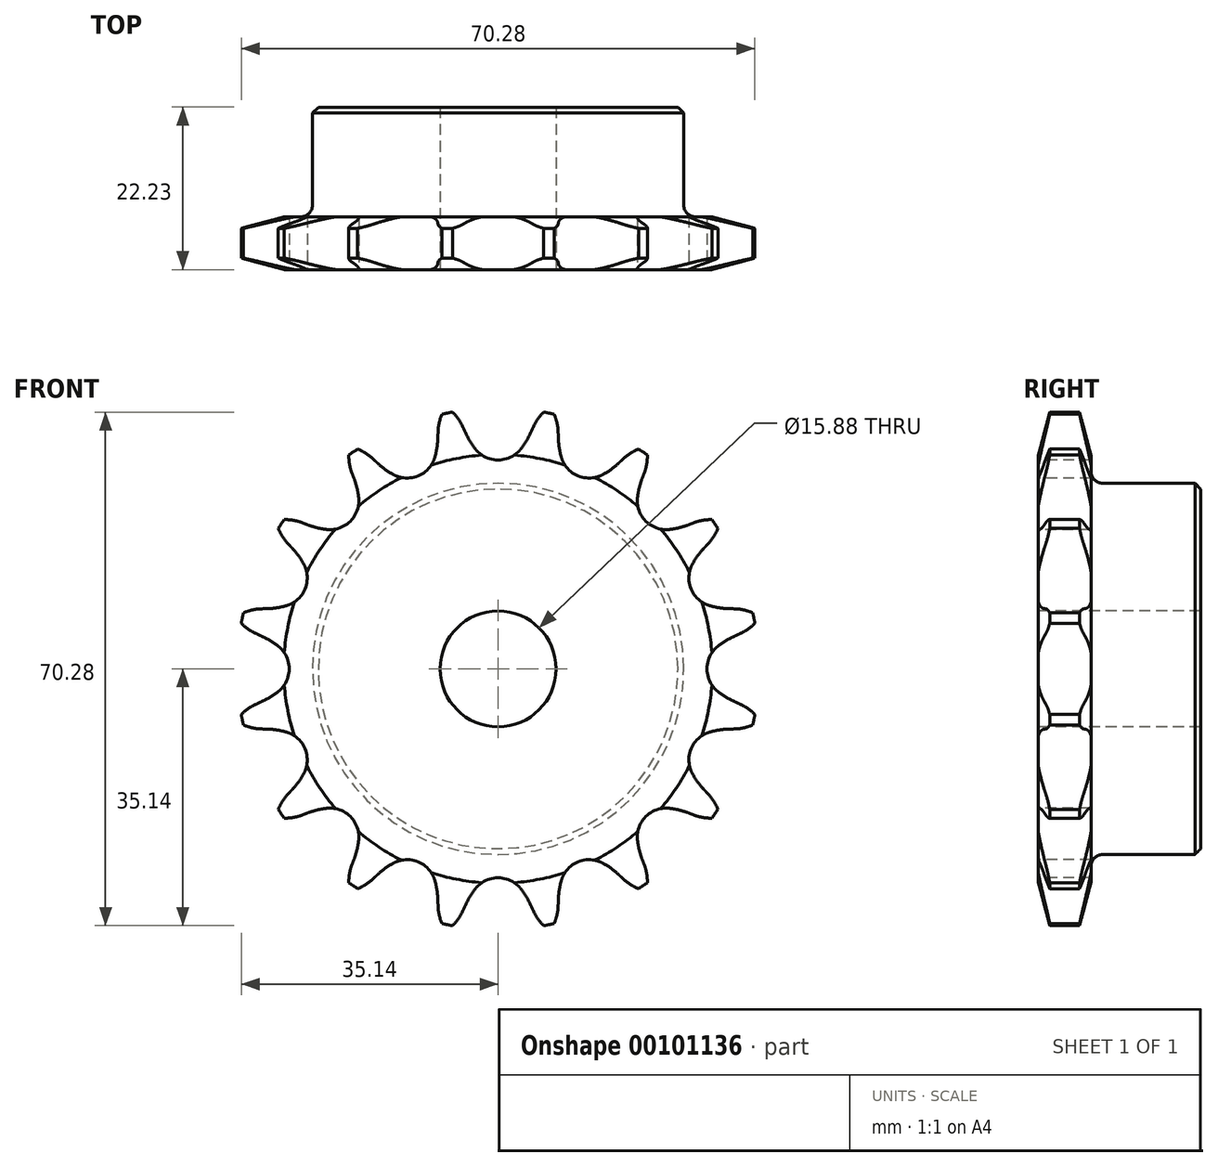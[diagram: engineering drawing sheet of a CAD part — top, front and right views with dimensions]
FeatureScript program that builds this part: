
annotation { "Feature Type Name" : "Feature", "Feature Type Description" : "" }
export const myFeature = defineFeature(function(context is Context, id is Id, definition is map)
    precondition{}
    {
        {
            var Q0;
            Q0=qCreatedBy(makeId("Right.planeOp"),FACE);
            var sketch = newSketch(context, id + "F0", { "sketchPlane" : qUnion([Q0])});
            skLineSegment(sketch, "E0", {"start": v(0, 0) * mm, "end": v(22.23, 0) * mm, "construction": true});
            skLineSegment(sketch, "E1.bottom", {"start": v(0, 7.94) * mm, "end": v(7.21, 7.94) * mm});
            skLineSegment(sketch, "E1.top", {"start": v(0, 35.69) * mm, "end": v(7.21, 35.69) * mm});
            skLineSegment(sketch, "E1.left", {"start": v(0, 7.94) * mm, "end": v(0, 35.69) * mm});
            skLineSegment(sketch, "E1.right", {"start": v(7.21, 7.94) * mm, "end": v(7.21, 35.69) * mm});
            skLineSegment(sketch, "E2.bottom", {"start": v(0, 7.94) * mm, "end": v(22.23, 7.94) * mm});
            skLineSegment(sketch, "E2.top", {"start": v(0, 25.4) * mm, "end": v(22.23, 25.4) * mm});
            skLineSegment(sketch, "E2.left", {"start": v(0, 7.94) * mm, "end": v(0, 25.4) * mm});
            skLineSegment(sketch, "E2.right", {"start": v(22.23, 7.94) * mm, "end": v(22.22, 25.4) * mm});
            skLineSegment(sketch, "E3.MirrorCS", {"start": v(0, -7.94) * mm, "end": v(7.21, -7.94) * mm});
            skLineSegment(sketch, "E4.MirrorCS", {"start": v(0, -7.94) * mm, "end": v(22.23, -7.94) * mm});
            skLineSegment(sketch, "E5.MirrorCS", {"start": v(0, -25.4) * mm, "end": v(22.23, -25.4) * mm});
            skLineSegment(sketch, "E6.MirrorCS", {"start": v(0, -7.94) * mm, "end": v(0, -25.4) * mm});
            skLineSegment(sketch, "E7.MirrorCS", {"start": v(22.23, -7.94) * mm, "end": v(22.23, -25.4) * mm});
            skLineSegment(sketch, "E8.MirrorCS", {"start": v(7.21, -7.94) * mm, "end": v(7.21, -35.69) * mm});
            skLineSegment(sketch, "E9.MirrorCS", {"start": v(0, -35.69) * mm, "end": v(7.21, -35.69) * mm});
            skLineSegment(sketch, "E10.MirrorCS", {"start": v(0, -7.94) * mm, "end": v(0, -35.69) * mm});
            skSolve(sketch);
        }
        {
            var Q0;
            {var subQ0=sQuery(id+"F0.wireOp",EDGE,"E1.top");Q0=makeQuery(id+"F0.imprint","IMPRINT",FACE,{"disambiguationData":[TD([[makeQuery(id+"F0.imprint","IMPRINT",EDGE,{"derivedFrom":subQ0}),-1.0]])]});}
            var Q1;
            {var subQ0=sQuery(id+"F0.wireOp",EDGE,"E1.bottom");Q1=makeQuery(id+"F0.imprint","IMPRINT",FACE,{"disambiguationData":[TD([[makeQuery(id+"F0.imprint","IMPRINT",EDGE,{"derivedFrom":subQ0}),1.0]])]});}
            var Q2;
            {var subQ0=sQuery(id+"F0.wireOp",EDGE,"E2.bottom");Q2=makeQuery(id+"F0.imprint","IMPRINT",FACE,{"disambiguationData":[TD([[makeQuery(id+"F0.imprint","IMPRINT",EDGE,{"derivedFrom":subQ0}),1.0]])]});}
            var Q3;
            Q3=sQuery(id+"F0.wireOp",EDGE,"E0");
            revolve(context, id + "F1", {"entities" : qUnion([Q0, Q1, Q2]), "axis" : qUnion([Q3]), "revolveType" : RevolveType.FULL});
        }
        {
            var Q0;
            Q0=makeQuery(id+"F1.opRevolve","SWEPT_EDGE",EDGE,{"disambiguationData":[OSD([sQuery(id+"F0.wireOp",EDGE,"E1.right"),sQuery(id+"F0.wireOp",EDGE,"E2.top")])]});
            fillet(context, id + "F2", {"entities" : qUnion([Q0]), "radius" : 1.59 * mm, "tangentPropagation" : true, "allowEdgeOverflow" : false});
        }
        {
            var Q0;
            Q0=makeQuery(id+"F1.opRevolve","SWEPT_EDGE",EDGE,{"disambiguationData":[OSD([sQuery(id+"F0.wireOp",EDGE,"E2.top"),sQuery(id+"F0.wireOp",EDGE,"E2.right")])]});
            chamfer(context, id + "F3", {"entities" : qUnion([Q0]), "width" : 0.8 * mm, "tangentPropagation" : true});
        }
        {
            var Q0;
            Q0=makeQuery(id+"F1.opRevolve","SWEPT_EDGE",EDGE,{"disambiguationData":[OSD([sQuery(id+"F0.wireOp",EDGE,"E1.top"),sQuery(id+"F0.wireOp",EDGE,"E1.left")])]});
            var Q1;
            Q1=makeQuery(id+"F1.opRevolve","SWEPT_EDGE",EDGE,{"disambiguationData":[OSD([sQuery(id+"F0.wireOp",EDGE,"E1.top"),sQuery(id+"F0.wireOp",EDGE,"E1.right")])]});
            chamfer(context, id + "F4", {"entities" : qUnion([Q0, Q1]), "chamferType" : ChamferType.TWO_OFFSETS, "width1" : 6.35 * mm, "oppositeDirection" : false, "width2" : 1.57 * mm, "tangentPropagation" : true});
        }
        {
            var Q0;
            Q0=makeQuery(id+"F1.opRevolve","SWEPT_FACE",FACE,{"disambiguationData":[OSD([sQuery(id+"F0.wireOp",EDGE,"E1.left")])]});
            var sketch = newSketch(context, id + "F5", { "sketchPlane" : qUnion([Q0])});
            skCircle(sketch, "E11", {"center": v(0, 0) * mm, "radius": 32.55 * mm, "construction": true});
            skLineSegment(sketch, "E12", {"start": v(0, 0) * mm, "end": v(0, 32.55) * mm, "construction": true});
            skLineSegment(sketch, "E13", {"start": v(31.36, 32.55) * mm, "end": v(0, 32.55) * mm, "construction": true});
            skLineSegment(sketch, "E14", {"start": v(0, 32.55) * mm, "end": v(5, 36.56) * mm, "construction": true});
            skLineSegment(sketch, "E15", {"start": v(5, 36.56) * mm, "end": v(-4.46, 32.3) * mm, "construction": true});
            skLineSegment(sketch, "E16", {"start": v(-4.46, 32.3) * mm, "end": v(-4.46, 32.3) * mm});
            skLineSegment(sketch, "E17", {"start": v(0, 0) * mm, "end": v(-7.13, 35.85) * mm, "construction": true});
            skArc(sketch, "E18", {"start": v(-7.13, 35.85) * mm, "mid": v(-15.87, 26.15) * mm, "end": v(-4.82, 33.1) * mm, "construction": true});
            skLineSegment(sketch, "E19", {"start": v(-4.82, 33.1) * mm, "end": v(-4.82, 33.1) * mm});
            skLineSegment(sketch, "E20", {"start": v(6.4, 8.22) * mm, "end": v(2.4, 17.08) * mm, "construction": true});
            skArc(sketch, "E21", {"start": v(-4.82, 33.1) * mm, "mid": v(-5.78, 34.63) * mm, "end": v(-7.13, 35.85) * mm});
            skLineSegment(sketch, "E22", {"start": v(-4.46, 32.3) * mm, "end": v(-4.82, 33.1) * mm});
            skLineSegment(sketch, "E23", {"start": v(6.4, 8.18) * mm, "end": v(6.4, 8.22) * mm, "construction": true});
            skLineSegment(sketch, "E24", {"start": v(-3.1, 30.07) * mm, "end": v(-3.1, 30.07) * mm});
            skArc(sketch, "E25", {"start": v(-4.46, 32.3) * mm, "mid": v(-3.84, 31.14) * mm, "end": v(-3.1, 30.07) * mm});
            skArc(sketch, "E26", {"start": v(-3.1, 30.07) * mm, "mid": v(-0.4, 27.71) * mm, "end": v(2.91, 26.4) * mm, "construction": true});
            skArc(sketch, "E27.MirrorCS", {"start": v(4.82, 33.1) * mm, "mid": v(5.78, 34.63) * mm, "end": v(7.13, 35.85) * mm});
            skLineSegment(sketch, "E28.MirrorCS", {"start": v(4.46, 32.3) * mm, "end": v(4.82, 33.1) * mm});
            skArc(sketch, "E29.MirrorCS", {"start": v(4.46, 32.3) * mm, "mid": v(3.84, 31.14) * mm, "end": v(3.1, 30.07) * mm});
            skArc(sketch, "E30", {"start": v(2.91, 26.4) * mm, "mid": v(11.47, 44.65) * mm, "end": v(-4.46, 32.3) * mm, "construction": true});
            skArc(sketch, "E31", {"start": v(-3.1, 30.07) * mm, "mid": v(0, 28.59) * mm, "end": v(3.1, 30.07) * mm});
            skArc(sketch, "E32", {"start": v(3.1, 30.07) * mm, "mid": v(0, 36.51) * mm, "end": v(-3.1, 30.07) * mm, "construction": true});
            skArc(sketch, "E33.1.0", {"start": v(-8.22, 32.42) * mm, "mid": v(-7.91, 34.21) * mm, "end": v(-7.13, 35.85) * mm});
            skLineSegment(sketch, "E33.1.1", {"start": v(-8.24, 31.55) * mm, "end": v(-8.22, 32.42) * mm});
            skArc(sketch, "E33.1.2", {"start": v(-8.24, 31.55) * mm, "mid": v(-8.37, 30.24) * mm, "end": v(-8.65, 28.96) * mm});
            skArc(sketch, "E33.1.3", {"start": v(-14.36, 26.6) * mm, "mid": v(-10.94, 26.41) * mm, "end": v(-8.65, 28.96) * mm});
            skArc(sketch, "E33.1.4", {"start": v(-16.48, 28.14) * mm, "mid": v(-15.47, 27.3) * mm, "end": v(-14.36, 26.6) * mm});
            skLineSegment(sketch, "E33.1.5", {"start": v(-16.48, 28.14) * mm, "end": v(-17.12, 28.74) * mm});
            skArc(sketch, "E33.1.6", {"start": v(-17.12, 28.74) * mm, "mid": v(-18.6, 29.79) * mm, "end": v(-20.3, 30.4) * mm});
            skArc(sketch, "E33.2.0", {"start": v(-20, 26.8) * mm, "mid": v(-20.4, 28.58) * mm, "end": v(-20.3, 30.4) * mm});
            skLineSegment(sketch, "E33.2.1", {"start": v(-19.69, 26) * mm, "end": v(-20, 26.8) * mm});
            skArc(sketch, "E33.2.2", {"start": v(-19.69, 26) * mm, "mid": v(-19.3, 24.74) * mm, "end": v(-19.08, 23.45) * mm});
            skArc(sketch, "E33.2.3", {"start": v(-23.45, 19.08) * mm, "mid": v(-20.21, 20.21) * mm, "end": v(-19.08, 23.45) * mm});
            skArc(sketch, "E33.2.4", {"start": v(-26, 19.69) * mm, "mid": v(-24.74, 19.3) * mm, "end": v(-23.45, 19.08) * mm});
            skLineSegment(sketch, "E33.2.5", {"start": v(-26, 19.69) * mm, "end": v(-26.8, 20) * mm});
            skArc(sketch, "E33.2.6", {"start": v(-26.8, 20) * mm, "mid": v(-28.58, 20.4) * mm, "end": v(-30.4, 20.3) * mm});
            skArc(sketch, "E33.3.0", {"start": v(-28.74, 17.12) * mm, "mid": v(-29.79, 18.6) * mm, "end": v(-30.4, 20.3) * mm});
            skLineSegment(sketch, "E33.3.1", {"start": v(-28.14, 16.48) * mm, "end": v(-28.74, 17.12) * mm});
            skArc(sketch, "E33.3.2", {"start": v(-28.14, 16.48) * mm, "mid": v(-27.3, 15.47) * mm, "end": v(-26.6, 14.36) * mm});
            skArc(sketch, "E33.3.3", {"start": v(-28.96, 8.65) * mm, "mid": v(-26.41, 10.94) * mm, "end": v(-26.6, 14.36) * mm});
            skArc(sketch, "E33.3.4", {"start": v(-31.55, 8.24) * mm, "mid": v(-30.24, 8.37) * mm, "end": v(-28.96, 8.65) * mm});
            skLineSegment(sketch, "E33.3.5", {"start": v(-31.55, 8.24) * mm, "end": v(-32.42, 8.22) * mm});
            skArc(sketch, "E33.3.6", {"start": v(-32.42, 8.22) * mm, "mid": v(-34.21, 7.91) * mm, "end": v(-35.85, 7.13) * mm});
            skArc(sketch, "E33.4.0", {"start": v(-33.1, 4.82) * mm, "mid": v(-34.63, 5.78) * mm, "end": v(-35.85, 7.13) * mm});
            skLineSegment(sketch, "E33.4.1", {"start": v(-32.3, 4.46) * mm, "end": v(-33.1, 4.82) * mm});
            skArc(sketch, "E33.4.2", {"start": v(-32.3, 4.46) * mm, "mid": v(-31.14, 3.84) * mm, "end": v(-30.07, 3.1) * mm});
            skArc(sketch, "E33.4.3", {"start": v(-30.07, -3.1) * mm, "mid": v(-28.59, 0) * mm, "end": v(-30.07, 3.1) * mm});
            skArc(sketch, "E33.4.4", {"start": v(-32.3, -4.46) * mm, "mid": v(-31.14, -3.84) * mm, "end": v(-30.07, -3.1) * mm});
            skLineSegment(sketch, "E33.4.5", {"start": v(-32.3, -4.46) * mm, "end": v(-33.1, -4.82) * mm});
            skArc(sketch, "E33.4.6", {"start": v(-33.1, -4.82) * mm, "mid": v(-34.63, -5.78) * mm, "end": v(-35.85, -7.13) * mm});
            skArc(sketch, "E33.5.0", {"start": v(-32.42, -8.22) * mm, "mid": v(-34.21, -7.91) * mm, "end": v(-35.85, -7.13) * mm});
            skLineSegment(sketch, "E33.5.1", {"start": v(-31.55, -8.24) * mm, "end": v(-32.42, -8.22) * mm});
            skArc(sketch, "E33.5.2", {"start": v(-31.55, -8.24) * mm, "mid": v(-30.24, -8.37) * mm, "end": v(-28.96, -8.65) * mm});
            skArc(sketch, "E33.5.3", {"start": v(-26.6, -14.36) * mm, "mid": v(-26.41, -10.94) * mm, "end": v(-28.96, -8.65) * mm});
            skArc(sketch, "E33.5.4", {"start": v(-28.14, -16.48) * mm, "mid": v(-27.3, -15.47) * mm, "end": v(-26.6, -14.36) * mm});
            skLineSegment(sketch, "E33.5.5", {"start": v(-28.14, -16.48) * mm, "end": v(-28.74, -17.12) * mm});
            skArc(sketch, "E33.5.6", {"start": v(-28.74, -17.12) * mm, "mid": v(-29.79, -18.6) * mm, "end": v(-30.4, -20.3) * mm});
            skArc(sketch, "E33.6.0", {"start": v(-26.8, -20) * mm, "mid": v(-28.58, -20.4) * mm, "end": v(-30.4, -20.3) * mm});
            skLineSegment(sketch, "E33.6.1", {"start": v(-26, -19.69) * mm, "end": v(-26.8, -20) * mm});
            skArc(sketch, "E33.6.2", {"start": v(-26, -19.69) * mm, "mid": v(-24.74, -19.3) * mm, "end": v(-23.45, -19.08) * mm});
            skArc(sketch, "E33.6.3", {"start": v(-19.08, -23.45) * mm, "mid": v(-20.21, -20.21) * mm, "end": v(-23.45, -19.08) * mm});
            skArc(sketch, "E33.6.4", {"start": v(-19.69, -26) * mm, "mid": v(-19.3, -24.74) * mm, "end": v(-19.08, -23.45) * mm});
            skLineSegment(sketch, "E33.6.5", {"start": v(-19.69, -26) * mm, "end": v(-20, -26.8) * mm});
            skArc(sketch, "E33.6.6", {"start": v(-20, -26.8) * mm, "mid": v(-20.4, -28.58) * mm, "end": v(-20.3, -30.4) * mm});
            skArc(sketch, "E33.7.0", {"start": v(-17.12, -28.74) * mm, "mid": v(-18.6, -29.79) * mm, "end": v(-20.3, -30.4) * mm});
            skLineSegment(sketch, "E33.7.1", {"start": v(-16.48, -28.14) * mm, "end": v(-17.12, -28.74) * mm});
            skArc(sketch, "E33.7.2", {"start": v(-16.48, -28.14) * mm, "mid": v(-15.47, -27.3) * mm, "end": v(-14.36, -26.6) * mm});
            skArc(sketch, "E33.7.3", {"start": v(-8.65, -28.96) * mm, "mid": v(-10.94, -26.41) * mm, "end": v(-14.36, -26.6) * mm});
            skArc(sketch, "E33.7.4", {"start": v(-8.24, -31.55) * mm, "mid": v(-8.37, -30.24) * mm, "end": v(-8.65, -28.96) * mm});
            skLineSegment(sketch, "E33.7.5", {"start": v(-8.24, -31.55) * mm, "end": v(-8.22, -32.42) * mm});
            skArc(sketch, "E33.7.6", {"start": v(-8.22, -32.42) * mm, "mid": v(-7.91, -34.21) * mm, "end": v(-7.13, -35.85) * mm});
            skArc(sketch, "E33.8.0", {"start": v(-4.82, -33.1) * mm, "mid": v(-5.78, -34.63) * mm, "end": v(-7.13, -35.85) * mm});
            skLineSegment(sketch, "E33.8.1", {"start": v(-4.46, -32.3) * mm, "end": v(-4.82, -33.1) * mm});
            skArc(sketch, "E33.8.2", {"start": v(-4.46, -32.3) * mm, "mid": v(-3.84, -31.14) * mm, "end": v(-3.1, -30.07) * mm});
            skArc(sketch, "E33.8.3", {"start": v(3.1, -30.07) * mm, "mid": v(0, -28.59) * mm, "end": v(-3.1, -30.07) * mm});
            skArc(sketch, "E33.8.4", {"start": v(4.46, -32.3) * mm, "mid": v(3.84, -31.14) * mm, "end": v(3.1, -30.07) * mm});
            skLineSegment(sketch, "E33.8.5", {"start": v(4.46, -32.3) * mm, "end": v(4.82, -33.1) * mm});
            skArc(sketch, "E33.8.6", {"start": v(4.82, -33.1) * mm, "mid": v(5.78, -34.63) * mm, "end": v(7.13, -35.85) * mm});
            skArc(sketch, "E33.9.0", {"start": v(8.22, -32.42) * mm, "mid": v(7.91, -34.21) * mm, "end": v(7.13, -35.85) * mm});
            skLineSegment(sketch, "E33.9.1", {"start": v(8.24, -31.55) * mm, "end": v(8.22, -32.42) * mm});
            skArc(sketch, "E33.9.2", {"start": v(8.24, -31.55) * mm, "mid": v(8.37, -30.24) * mm, "end": v(8.65, -28.96) * mm});
            skArc(sketch, "E33.9.3", {"start": v(14.36, -26.6) * mm, "mid": v(10.94, -26.41) * mm, "end": v(8.65, -28.96) * mm});
            skArc(sketch, "E33.9.4", {"start": v(16.48, -28.14) * mm, "mid": v(15.47, -27.3) * mm, "end": v(14.36, -26.6) * mm});
            skLineSegment(sketch, "E33.9.5", {"start": v(16.48, -28.14) * mm, "end": v(17.12, -28.74) * mm});
            skArc(sketch, "E33.9.6", {"start": v(17.12, -28.74) * mm, "mid": v(18.6, -29.79) * mm, "end": v(20.3, -30.4) * mm});
            skArc(sketch, "E33.10.0", {"start": v(20, -26.8) * mm, "mid": v(20.4, -28.58) * mm, "end": v(20.3, -30.4) * mm});
            skLineSegment(sketch, "E33.10.1", {"start": v(19.69, -26) * mm, "end": v(20, -26.8) * mm});
            skArc(sketch, "E33.10.2", {"start": v(19.69, -26) * mm, "mid": v(19.3, -24.74) * mm, "end": v(19.08, -23.45) * mm});
            skArc(sketch, "E33.10.3", {"start": v(23.45, -19.08) * mm, "mid": v(20.21, -20.21) * mm, "end": v(19.08, -23.45) * mm});
            skArc(sketch, "E33.10.4", {"start": v(26, -19.69) * mm, "mid": v(24.74, -19.3) * mm, "end": v(23.45, -19.08) * mm});
            skLineSegment(sketch, "E33.10.5", {"start": v(26, -19.69) * mm, "end": v(26.8, -20) * mm});
            skArc(sketch, "E33.10.6", {"start": v(26.8, -20) * mm, "mid": v(28.58, -20.4) * mm, "end": v(30.4, -20.3) * mm});
            skArc(sketch, "E33.11.0", {"start": v(28.74, -17.12) * mm, "mid": v(29.79, -18.6) * mm, "end": v(30.4, -20.3) * mm});
            skLineSegment(sketch, "E33.11.1", {"start": v(28.14, -16.48) * mm, "end": v(28.74, -17.12) * mm});
            skArc(sketch, "E33.11.2", {"start": v(28.14, -16.48) * mm, "mid": v(27.3, -15.47) * mm, "end": v(26.6, -14.36) * mm});
            skArc(sketch, "E33.11.3", {"start": v(28.96, -8.65) * mm, "mid": v(26.41, -10.94) * mm, "end": v(26.6, -14.36) * mm});
            skArc(sketch, "E33.11.4", {"start": v(31.55, -8.24) * mm, "mid": v(30.24, -8.37) * mm, "end": v(28.96, -8.65) * mm});
            skLineSegment(sketch, "E33.11.5", {"start": v(31.55, -8.24) * mm, "end": v(32.42, -8.22) * mm});
            skArc(sketch, "E33.11.6", {"start": v(32.42, -8.22) * mm, "mid": v(34.21, -7.91) * mm, "end": v(35.85, -7.13) * mm});
            skArc(sketch, "E33.12.0", {"start": v(33.1, -4.82) * mm, "mid": v(34.63, -5.78) * mm, "end": v(35.85, -7.13) * mm});
            skLineSegment(sketch, "E33.12.1", {"start": v(32.3, -4.46) * mm, "end": v(33.1, -4.82) * mm});
            skArc(sketch, "E33.12.2", {"start": v(32.3, -4.46) * mm, "mid": v(31.14, -3.84) * mm, "end": v(30.07, -3.1) * mm});
            skArc(sketch, "E33.12.3", {"start": v(30.07, 3.1) * mm, "mid": v(28.59, 0) * mm, "end": v(30.07, -3.1) * mm});
            skArc(sketch, "E33.12.4", {"start": v(32.3, 4.46) * mm, "mid": v(31.14, 3.84) * mm, "end": v(30.07, 3.1) * mm});
            skLineSegment(sketch, "E33.12.5", {"start": v(32.3, 4.46) * mm, "end": v(33.1, 4.82) * mm});
            skArc(sketch, "E33.12.6", {"start": v(33.1, 4.82) * mm, "mid": v(34.63, 5.78) * mm, "end": v(35.85, 7.13) * mm});
            skArc(sketch, "E33.13.0", {"start": v(32.42, 8.22) * mm, "mid": v(34.21, 7.91) * mm, "end": v(35.85, 7.13) * mm});
            skLineSegment(sketch, "E33.13.1", {"start": v(31.55, 8.24) * mm, "end": v(32.42, 8.22) * mm});
            skArc(sketch, "E33.13.2", {"start": v(31.55, 8.24) * mm, "mid": v(30.24, 8.37) * mm, "end": v(28.96, 8.65) * mm});
            skArc(sketch, "E33.13.3", {"start": v(26.6, 14.36) * mm, "mid": v(26.41, 10.94) * mm, "end": v(28.96, 8.65) * mm});
            skArc(sketch, "E33.13.4", {"start": v(28.14, 16.48) * mm, "mid": v(27.3, 15.47) * mm, "end": v(26.6, 14.36) * mm});
            skLineSegment(sketch, "E33.13.5", {"start": v(28.14, 16.48) * mm, "end": v(28.74, 17.12) * mm});
            skArc(sketch, "E33.13.6", {"start": v(28.74, 17.12) * mm, "mid": v(29.79, 18.6) * mm, "end": v(30.4, 20.3) * mm});
            skArc(sketch, "E33.14.0", {"start": v(26.8, 20) * mm, "mid": v(28.58, 20.4) * mm, "end": v(30.4, 20.3) * mm});
            skLineSegment(sketch, "E33.14.1", {"start": v(26, 19.69) * mm, "end": v(26.8, 20) * mm});
            skArc(sketch, "E33.14.2", {"start": v(26, 19.69) * mm, "mid": v(24.74, 19.3) * mm, "end": v(23.45, 19.08) * mm});
            skArc(sketch, "E33.14.3", {"start": v(19.08, 23.45) * mm, "mid": v(20.21, 20.21) * mm, "end": v(23.45, 19.08) * mm});
            skArc(sketch, "E33.14.4", {"start": v(19.69, 26) * mm, "mid": v(19.3, 24.74) * mm, "end": v(19.08, 23.45) * mm});
            skLineSegment(sketch, "E33.14.5", {"start": v(19.69, 26) * mm, "end": v(20, 26.8) * mm});
            skArc(sketch, "E33.14.6", {"start": v(20, 26.8) * mm, "mid": v(20.4, 28.58) * mm, "end": v(20.3, 30.4) * mm});
            skArc(sketch, "E33.15.0", {"start": v(17.12, 28.74) * mm, "mid": v(18.6, 29.79) * mm, "end": v(20.3, 30.4) * mm});
            skLineSegment(sketch, "E33.15.1", {"start": v(16.48, 28.14) * mm, "end": v(17.12, 28.74) * mm});
            skArc(sketch, "E33.15.2", {"start": v(16.48, 28.14) * mm, "mid": v(15.47, 27.3) * mm, "end": v(14.36, 26.6) * mm});
            skArc(sketch, "E33.15.3", {"start": v(8.65, 28.96) * mm, "mid": v(10.94, 26.41) * mm, "end": v(14.36, 26.6) * mm});
            skArc(sketch, "E33.15.4", {"start": v(8.24, 31.55) * mm, "mid": v(8.37, 30.24) * mm, "end": v(8.65, 28.96) * mm});
            skLineSegment(sketch, "E33.15.5", {"start": v(8.24, 31.55) * mm, "end": v(8.22, 32.42) * mm});
            skArc(sketch, "E33.15.6", {"start": v(8.22, 32.42) * mm, "mid": v(7.91, 34.21) * mm, "end": v(7.13, 35.85) * mm});
            skSolve(sketch);
        }
        {
            var Q0;
            Q0 = qSketchRegion(id + "F5", true);
            extrude(context, id + "F6", {"entities" : qUnion([Q0]), "operationType" : NewBodyOperationType.INTERSECT, "endBound" : BoundingType.THROUGH_ALL, "oppositeDirection" : true, "depth" : 25.4 * mm});
        }
    });
